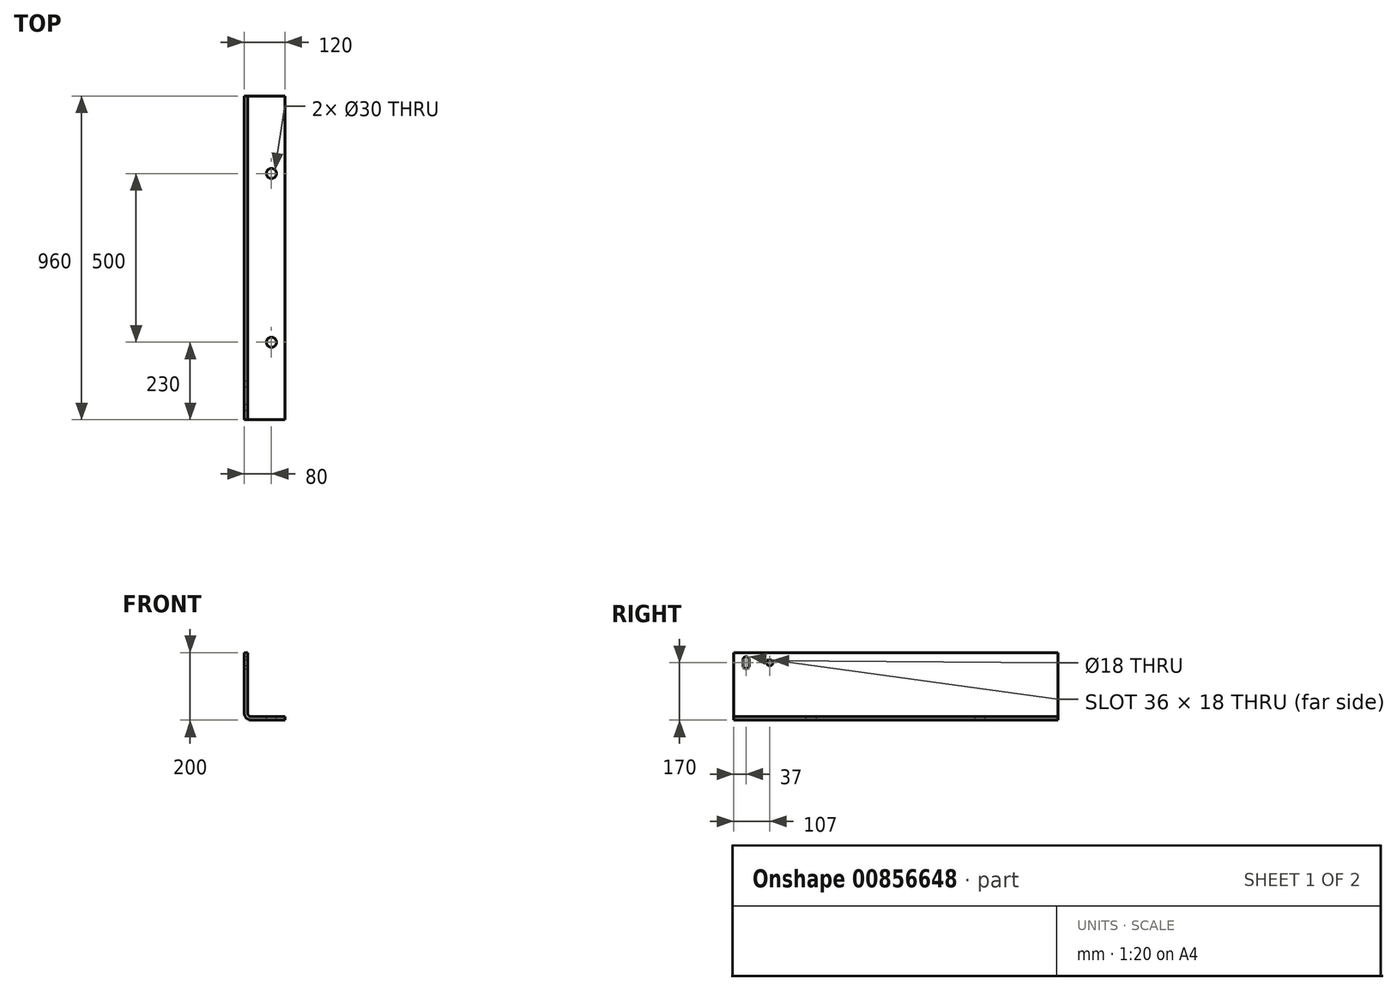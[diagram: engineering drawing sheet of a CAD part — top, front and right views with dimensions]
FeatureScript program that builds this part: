
annotation { "Feature Type Name" : "Feature", "Feature Type Description" : "" }
export const myFeature = defineFeature(function(context is Context, id is Id, definition is map)
    precondition{}
    {
        {
            var Q0;
            Q0=qCreatedBy(makeId("Front.planeOp"),FACE);
            var sketch = newSketch(context, id + "F0", { "sketchPlane" : qUnion([Q0])});
            skLineSegment(sketch, "E0", {"start": v(0, 0) * mm, "end": v(120, 0) * mm});
            skLineSegment(sketch, "E1", {"start": v(0, 0) * mm, "end": v(0, 200) * mm});
            skLineSegment(sketch, "E2.0", {"start": v(10, 10) * mm, "end": v(120, 10) * mm});
            skLineSegment(sketch, "E2.1", {"start": v(10, 10) * mm, "end": v(10, 200) * mm});
            skLineSegment(sketch, "E3", {"start": v(10, 200) * mm, "end": v(0, 200) * mm});
            skLineSegment(sketch, "E4", {"start": v(120, 0) * mm, "end": v(120, 10) * mm});
            skSolve(sketch);
        }
        {
            var Q0;
            Q0 = qSketchRegion(id + "F0", true);
            extrude(context, id + "F1", {"entities" : qUnion([Q0]), "endBound" : BoundingType.SYMMETRIC, "depth" : 960 * mm, "offsetDistance" : 25 * mm});
        }
        {
            var Q0;
            Q0=makeQuery(id+"F1.opExtrude","SWEPT_FACE",FACE,{"disambiguationData":[OSD([sQuery(id+"F0.wireOp",EDGE,"E2.1")])]});
            var sketch = newSketch(context, id + "F2", { "sketchPlane" : qUnion([Q0])});
            skLineSegment(sketch, "E5", {"start": v(-480, 170) * mm, "end": v(480, 170) * mm, "construction": true});
            skLineSegment(sketch, "E6.bottom", {"start": v(-434, 188) * mm, "end": v(-452, 188) * mm});
            skLineSegment(sketch, "E6.top", {"start": v(-434, 152) * mm, "end": v(-452, 152) * mm});
            skLineSegment(sketch, "E6.left", {"start": v(-434, 188) * mm, "end": v(-434, 152) * mm});
            skLineSegment(sketch, "E6.right", {"start": v(-452, 188) * mm, "end": v(-452, 152) * mm});
            skPoint(sketch, "E6.middle", {"position": v(-443, 170) * mm});
            skLineSegment(sketch, "E7", {"start": v(-452, 179) * mm, "end": v(-434, 179) * mm, "construction": true});
            skArc(sketch, "E8", {"start": v(-434, 179) * mm, "mid": v(-443, 188) * mm, "end": v(-452, 179) * mm});
            skArc(sketch, "E9.MirrorCS", {"start": v(-434, 161) * mm, "mid": v(-443, 152) * mm, "end": v(-452, 161) * mm});
            skArc(sketch, "E10.MirrorCS", {"start": v(434, 179) * mm, "mid": v(443, 188) * mm, "end": v(452, 179) * mm});
            skArc(sketch, "E11.MirrorCS", {"start": v(434, 161) * mm, "mid": v(443, 152) * mm, "end": v(452, 161) * mm});
            skLineSegment(sketch, "E12.MirrorCS", {"start": v(434, 188) * mm, "end": v(434, 152) * mm});
            skLineSegment(sketch, "E13.MirrorCS", {"start": v(452, 188) * mm, "end": v(452, 152) * mm});
            skLineSegment(sketch, "E14.MirrorCS", {"start": v(434, 188) * mm, "end": v(452, 188) * mm});
            skLineSegment(sketch, "E15.MirrorCS", {"start": v(434, 152) * mm, "end": v(452, 152) * mm});
            skLineSegment(sketch, "E16", {"start": v(-408, 200) * mm, "end": v(-408, 170) * mm, "construction": true});
            skPoint(sketch, "E17.MirrorP", {"position": v(-373, 170) * mm});
            skCircle(sketch, "E18", {"center": v(-373, 170) * mm, "radius": 9 * mm});
            skSolve(sketch);
        }
        {
            var Q0;
            Q0=makeQuery(id+"F2.imprint","IMPRINT",FACE,{"disambiguationData":[TD([[makeQuery(id+"F2.imprint","IMPRINT",EDGE,{"derivedFrom":sQuery(id+"F2.wireOp",EDGE,"E18")}),1.0]])]});
            var Q1;
            {var subQ0=sQuery(id+"F2.wireOp",EDGE,"E8");var subQ6=sQuery(id+"F2.wireOp",EDGE,"E6.left");var subQ7=makeQuery(id+"F2.imprint","INTERSECT",VERTEX,{"derivedFrom":[subQ6,subQ0]});Q1=makeQuery(id+"F2.imprint","IMPRINT",FACE,{"disambiguationData":[TD([[makeQuery(id+"F2.imprint","IMPRINT",EDGE,{"disambiguationData":[TD([[subQ7,-1.0]])],"derivedFrom":subQ6}),-1.0]])]});}
            var Q2;
            {var subQ4=sQuery(id+"F2.wireOp",EDGE,"E12.MirrorCS");var subQ6=sQuery(id+"F2.wireOp",EDGE,"E10.MirrorCS");var subQ9=makeQuery(id+"F2.imprint","INTERSECT",VERTEX,{"derivedFrom":[subQ6,subQ4]});Q2=makeQuery(id+"F2.imprint","IMPRINT",FACE,{"disambiguationData":[TD([[makeQuery(id+"F2.imprint","IMPRINT",EDGE,{"disambiguationData":[TD([[subQ9,-1.0]])],"derivedFrom":subQ6}),-1.0]])]});}
            extrude(context, id + "F3", {"entities" : qUnion([Q0, Q1, Q2]), "operationType" : NewBodyOperationType.REMOVE, "endBound" : BoundingType.UP_TO_NEXT, "oppositeDirection" : true, "depth" : 25 * mm, "offsetDistance" : 25 * mm});
        }
        {
            var Q0;
            Q0=makeQuery(id+"F1.opExtrude","SWEPT_FACE",FACE,{"disambiguationData":[OSD([sQuery(id+"F0.wireOp",EDGE,"E2.0")])]});
            var sketch = newSketch(context, id + "F4", { "sketchPlane" : qUnion([Q0])});
            skLineSegment(sketch, "E19", {"start": v(80, 480) * mm, "end": v(80, -480) * mm, "construction": true});
            skPoint(sketch, "E20", {"position": v(80, -250) * mm});
            skCircle(sketch, "E21", {"center": v(80, -250) * mm, "radius": 15 * mm});
            skCircle(sketch, "E22.MirrorC", {"center": v(80, 250) * mm, "radius": 15 * mm});
            skSolve(sketch);
        }
        {
            var Q0;
            Q0 = qSketchRegion(id + "F4", true);
            extrude(context, id + "F5", {"entities" : qUnion([Q0]), "operationType" : NewBodyOperationType.REMOVE, "endBound" : BoundingType.UP_TO_NEXT, "oppositeDirection" : true, "depth" : 25 * mm, "offsetDistance" : 25 * mm});
        }
        {
            var Q0;
            Q0=makeQuery(id+"F1.opExtrude","SWEPT_EDGE",EDGE,{"disambiguationData":[OSD([sQuery(id+"F0.wireOp",EDGE,"E2.0"),sQuery(id+"F0.wireOp",EDGE,"E2.1")])]});
            fillet(context, id + "F6", {"entities" : qUnion([Q0]), "radius" : 10 * mm, "tangentPropagation" : true, "allowEdgeOverflow" : false});
        }
        {
            var Q0;
            Q0=makeQuery(id+"F1.opExtrude","SWEPT_EDGE",EDGE,{"disambiguationData":[OSD([sQuery(id+"F0.wireOp",EDGE,"E0"),sQuery(id+"F0.wireOp",EDGE,"E1")])]});
            fillet(context, id + "F7", {"entities" : qUnion([Q0]), "radius" : 20 * mm, "tangentPropagation" : true, "allowEdgeOverflow" : false});
        }
    });
